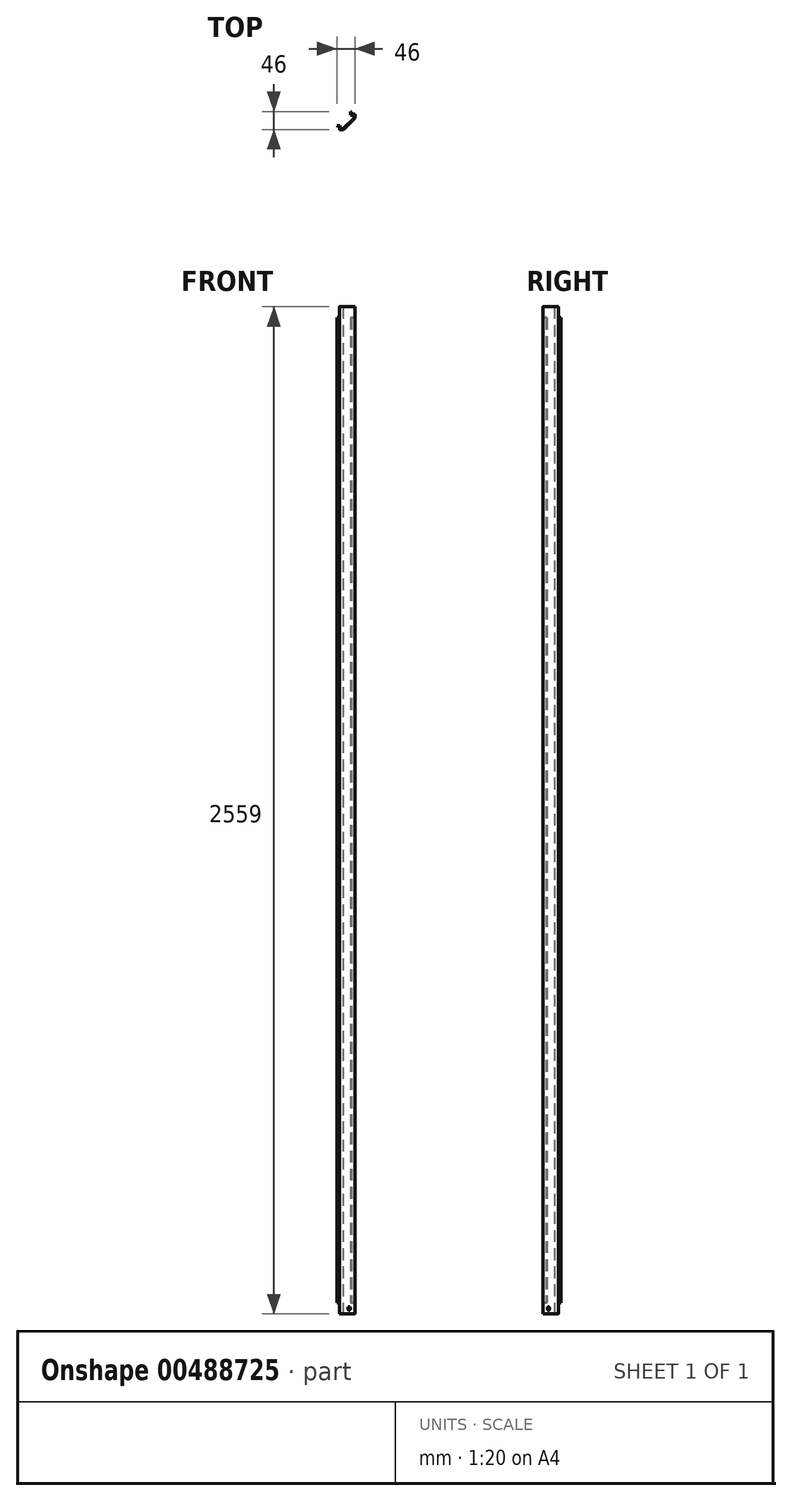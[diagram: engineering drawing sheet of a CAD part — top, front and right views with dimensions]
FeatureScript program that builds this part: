
annotation { "Feature Type Name" : "Feature", "Feature Type Description" : "" }
export const myFeature = defineFeature(function(context is Context, id is Id, definition is map)
    precondition{}
    {
        {
            var Q0;
            Q0=qCreatedBy(makeId("Top.planeOp"),FACE);
            var sketch = newSketch(context, id + "F0", { "sketchPlane" : qUnion([Q0])});
            skLineSegment(sketch, "E0", {"start": v(-68.1, 0) * mm, "end": v(72.16, 0) * mm, "construction": true});
            skLineSegment(sketch, "E1", {"start": v(0, 70.28) * mm, "end": v(0, -61.88) * mm, "construction": true});
            skLineSegment(sketch, "E2.bottom", {"start": v(-19.75, 19.75) * mm, "end": v(19.75, 19.75) * mm, "construction": true});
            skLineSegment(sketch, "E2.top", {"start": v(-19.75, -19.75) * mm, "end": v(19.75, -19.75) * mm, "construction": true});
            skLineSegment(sketch, "E2.left", {"start": v(-19.75, 19.75) * mm, "end": v(-19.75, -19.75) * mm, "construction": true});
            skLineSegment(sketch, "E2.right", {"start": v(19.75, 19.75) * mm, "end": v(19.75, -19.75) * mm, "construction": true});
            skLineSegment(sketch, "E3", {"start": v(-19.75, -19.75) * mm, "end": v(-9.25, -19.75) * mm});
            skLineSegment(sketch, "E4", {"start": v(19.75, 19.75) * mm, "end": v(19.75, 9.25) * mm});
            skLineSegment(sketch, "E5", {"start": v(-9.25, -19.75) * mm, "end": v(19.75, 9.25) * mm});
            skLineSegment(sketch, "E6.0", {"start": v(-19.75, -17.75) * mm, "end": v(-10.08, -17.75) * mm});
            skLineSegment(sketch, "E6.1", {"start": v(-10.08, -17.75) * mm, "end": v(17.75, 10.08) * mm});
            skLineSegment(sketch, "E6.2", {"start": v(17.75, 19.75) * mm, "end": v(17.75, 10.08) * mm});
            skLineSegment(sketch, "E7", {"start": v(-19.75, -19.75) * mm, "end": v(-19.75, -17.75) * mm});
            skLineSegment(sketch, "E8", {"start": v(19.75, 19.75) * mm, "end": v(17.75, 19.75) * mm});
            skSolve(sketch);
        }
        {
            var Q0;
            Q0=qSketchRegion(id+"F0",true);
            extrude(context, id + "F1", {"entities" : qUnion([Q0]), "depth" : 28 * mm});
        }
        {
            var Q0;
            Q0=makeQuery(id+"F1.opExtrude","CAP_FACE",FACE,{"disambiguationData":[OSD([sQuery(id+"F0.wireOp",EDGE,"E3"),sQuery(id+"F0.wireOp",EDGE,"E4"),sQuery(id+"F0.wireOp",EDGE,"E5"),sQuery(id+"F0.wireOp",EDGE,"E6.0"),sQuery(id+"F0.wireOp",EDGE,"E6.1"),sQuery(id+"F0.wireOp",EDGE,"E6.2"),sQuery(id+"F0.wireOp",EDGE,"E7"),sQuery(id+"F0.wireOp",EDGE,"E8")])],"isStart":false});
            var sketch = newSketch(context, id + "F2", { "sketchPlane" : qUnion([Q0])});
            skLineSegment(sketch, "E9.1", {"start": v(-9.25, -19.75) * mm, "end": v(19.75, 9.25) * mm});
            skLineSegment(sketch, "E9.2", {"start": v(19.75, 19.75) * mm, "end": v(19.75, 9.25) * mm});
            skLineSegment(sketch, "E10", {"start": v(19.75, 19.75) * mm, "end": v(11.25, 19.75) * mm});
            skLineSegment(sketch, "E11", {"start": v(17.75, 17.75) * mm, "end": v(17.75, 10.08) * mm});
            skLineSegment(sketch, "E12", {"start": v(17.75, 10.08) * mm, "end": v(16.59, 8.91) * mm});
            skLineSegment(sketch, "E13.left", {"start": v(11.25, 19.75) * mm, "end": v(11.25, 24.25) * mm});
            skLineSegment(sketch, "E14", {"start": v(11.25, 24.25) * mm, "end": v(9.25, 26.25) * mm});
            skLineSegment(sketch, "E15.trimOffspring", {"start": v(16.59, 8.91) * mm, "end": v(-8.91, -16.59) * mm});
            skLineSegment(sketch, "E16.0", {"start": v(9.25, 19.75) * mm, "end": v(9.25, 23.42) * mm});
            skLineSegment(sketch, "E17.0", {"start": v(9.25, 23.42) * mm, "end": v(9.25, 23.42) * mm});
            skLineSegment(sketch, "E18.trimOffspring", {"start": v(9.25, 23.42) * mm, "end": v(9.25, 26.25) * mm});
            skLineSegment(sketch, "E19", {"start": v(0, 0) * mm, "end": v(5.25, -5.25) * mm, "construction": true});
            skLineSegment(sketch, "E20.MirrorCS", {"start": v(-19.75, -9.25) * mm, "end": v(-23.42, -9.25) * mm});
            skLineSegment(sketch, "E21.MirrorCS", {"start": v(-19.75, -11.25) * mm, "end": v(-24.25, -11.25) * mm});
            skLineSegment(sketch, "E22.MirrorCS", {"start": v(-23.42, -9.25) * mm, "end": v(-26.25, -9.25) * mm});
            skLineSegment(sketch, "E23.MirrorCS", {"start": v(-19.75, -19.75) * mm, "end": v(-9.25, -19.75) * mm});
            skLineSegment(sketch, "E24.MirrorCS", {"start": v(-10.08, -17.75) * mm, "end": v(-8.91, -16.59) * mm});
            skLineSegment(sketch, "E25.MirrorCS", {"start": v(-24.25, -11.25) * mm, "end": v(-26.25, -9.25) * mm});
            skLineSegment(sketch, "E26.MirrorCS", {"start": v(-17.75, -17.75) * mm, "end": v(-10.08, -17.75) * mm});
            skLineSegment(sketch, "E27.MirrorCS", {"start": v(-23.42, -9.25) * mm, "end": v(-23.42, -9.25) * mm});
            skLineSegment(sketch, "E28.MirrorCS", {"start": v(-19.75, -19.75) * mm, "end": v(-19.75, -11.25) * mm});
            skLineSegment(sketch, "E29.trimOffspring", {"start": v(-8.91, -16.59) * mm, "end": v(-10.08, -17.75) * mm});
            skLineSegment(sketch, "E30", {"start": v(9.25, 19.75) * mm, "end": v(9.25, 17.75) * mm});
            skLineSegment(sketch, "E31", {"start": v(9.25, 17.75) * mm, "end": v(17.75, 17.75) * mm});
            skLineSegment(sketch, "E32", {"start": v(-19.75, -9.25) * mm, "end": v(-17.75, -9.25) * mm});
            skLineSegment(sketch, "E33", {"start": v(-17.75, -9.25) * mm, "end": v(-17.75, -17.75) * mm});
            skSolve(sketch);
        }
        {
            var Q0;
            Q0=qSketchRegion(id+"F2",true);
            extrude(context, id + "F3", {"entities" : qUnion([Q0]), "operationType" : NewBodyOperationType.ADD, "depth" : 2503 * mm, "offsetDistance" : 25 * mm});
        }
        {
            var Q0;
            Q0=makeQuery(id+"F3.opExtrude","CAP_FACE",FACE,{"disambiguationData":[OSD([sQuery(id+"F2.wireOp",EDGE,"E9.1"),sQuery(id+"F2.wireOp",EDGE,"E9.2"),sQuery(id+"F2.wireOp",EDGE,"E10"),sQuery(id+"F2.wireOp",EDGE,"E11"),sQuery(id+"F2.wireOp",EDGE,"E12"),sQuery(id+"F2.wireOp",EDGE,"E13.left"),sQuery(id+"F2.wireOp",EDGE,"E14"),sQuery(id+"F2.wireOp",EDGE,"E15.trimOffspring"),sQuery(id+"F2.wireOp",EDGE,"E16.0"),sQuery(id+"F2.wireOp",EDGE,"E17.0"),sQuery(id+"F2.wireOp",EDGE,"E18.trimOffspring"),sQuery(id+"F2.wireOp",EDGE,"E20.MirrorCS"),sQuery(id+"F2.wireOp",EDGE,"E21.MirrorCS"),sQuery(id+"F2.wireOp",EDGE,"E22.MirrorCS"),sQuery(id+"F2.wireOp",EDGE,"E23.MirrorCS"),sQuery(id+"F2.wireOp",EDGE,"E25.MirrorCS"),sQuery(id+"F2.wireOp",EDGE,"E26.MirrorCS"),sQuery(id+"F2.wireOp",EDGE,"E27.MirrorCS"),sQuery(id+"F2.wireOp",EDGE,"E28.MirrorCS"),sQuery(id+"F2.wireOp",EDGE,"E29.trimOffspring"),sQuery(id+"F2.wireOp",EDGE,"E30"),sQuery(id+"F2.wireOp",EDGE,"E31"),sQuery(id+"F2.wireOp",EDGE,"E32"),sQuery(id+"F2.wireOp",EDGE,"E33")])],"isStart":false});
            var sketch = newSketch(context, id + "F4", { "sketchPlane" : qUnion([Q0])});
            skLineSegment(sketch, "E34.0.0", {"start": v(19.75, 19.75) * mm, "end": v(19.75, 9.25) * mm});
            skLineSegment(sketch, "E34.0.1", {"start": v(19.75, 9.25) * mm, "end": v(-9.25, -19.75) * mm});
            skLineSegment(sketch, "E34.0.2", {"start": v(-9.25, -19.75) * mm, "end": v(-19.75, -19.75) * mm});
            skLineSegment(sketch, "E34.0.3", {"start": v(-19.75, -19.75) * mm, "end": v(-19.75, -17.75) * mm});
            skLineSegment(sketch, "E34.0.4", {"start": v(-19.75, -17.75) * mm, "end": v(-10.08, -17.75) * mm});
            skLineSegment(sketch, "E34.0.5", {"start": v(-10.08, -17.75) * mm, "end": v(17.75, 10.08) * mm});
            skLineSegment(sketch, "E34.0.6", {"start": v(17.75, 10.08) * mm, "end": v(17.75, 19.75) * mm});
            skLineSegment(sketch, "E34.0.7", {"start": v(17.75, 19.75) * mm, "end": v(19.75, 19.75) * mm});
            skSolve(sketch);
        }
        {
            var Q0;
            Q0 = qSketchRegion(id + "F4", true);
            extrude(context, id + "F5", {"entities" : qUnion([Q0]), "operationType" : NewBodyOperationType.ADD, "depth" : 28 * mm});
        }
        {
            var Q0;
            Q0=makeQuery(id+"F5.boolean.opBoolean","MERGE",EDGE,{"derivedFrom":[makeQuery(id+"F3.boolean.opBoolean","MERGE",EDGE,{"derivedFrom":[makeQuery(id+"F1.opExtrude","SWEPT_EDGE",EDGE,{"disambiguationData":[OSD([sQuery(id+"F0.wireOp",EDGE,"E4"),sQuery(id+"F0.wireOp",EDGE,"E5")])]}),makeQuery(id+"F3.opExtrude","SWEPT_EDGE",EDGE,{"disambiguationData":[OSD([sQuery(id+"F2.wireOp",EDGE,"E9.1"),sQuery(id+"F2.wireOp",EDGE,"E9.2")])]})]}),makeQuery(id+"F5.opExtrude","SWEPT_EDGE",EDGE,{"disambiguationData":[OSD([sQuery(id+"F4.wireOp",EDGE,"E34.0.0"),sQuery(id+"F4.wireOp",EDGE,"E34.0.1")])]})]});
            var Q1;
            Q1=makeQuery(id+"F5.boolean.opBoolean","MERGE",EDGE,{"derivedFrom":[makeQuery(id+"F3.boolean.opBoolean","MERGE",EDGE,{"derivedFrom":[makeQuery(id+"F1.opExtrude","SWEPT_EDGE",EDGE,{"disambiguationData":[OSD([sQuery(id+"F0.wireOp",EDGE,"E3"),sQuery(id+"F0.wireOp",EDGE,"E5")])]}),makeQuery(id+"F3.opExtrude","SWEPT_EDGE",EDGE,{"disambiguationData":[OSD([sQuery(id+"F2.wireOp",EDGE,"E9.1"),sQuery(id+"F2.wireOp",EDGE,"E23.MirrorCS")])]})]}),makeQuery(id+"F5.opExtrude","SWEPT_EDGE",EDGE,{"disambiguationData":[OSD([sQuery(id+"F4.wireOp",EDGE,"E34.0.1"),sQuery(id+"F4.wireOp",EDGE,"E34.0.2")])]})]});
            fillet(context, id + "F6", {"entities" : qUnion([Q0, Q1]), "radius" : 2 * mm, "tangentPropagation" : true, "allowEdgeOverflow" : false});
        }
        {
            var Q0;
            Q0=makeQuery(id+"F5.boolean.opBoolean","MERGE",EDGE,{"derivedFrom":[makeQuery(id+"F3.boolean.opBoolean","MERGE",EDGE,{"derivedFrom":[makeQuery(id+"F1.opExtrude","SWEPT_EDGE",EDGE,{"disambiguationData":[OSD([sQuery(id+"F0.wireOp",EDGE,"E3"),sQuery(id+"F0.wireOp",EDGE,"E7")])]}),makeQuery(id+"F3.opExtrude","SWEPT_EDGE",EDGE,{"disambiguationData":[OSD([sQuery(id+"F2.wireOp",EDGE,"E23.MirrorCS"),sQuery(id+"F2.wireOp",EDGE,"E28.MirrorCS")])]})]}),makeQuery(id+"F5.opExtrude","SWEPT_EDGE",EDGE,{"disambiguationData":[OSD([sQuery(id+"F4.wireOp",EDGE,"E34.0.2"),sQuery(id+"F4.wireOp",EDGE,"E34.0.3")])]})]});
            var Q1;
            Q1=makeQuery(id+"F5.boolean.opBoolean","MERGE",EDGE,{"derivedFrom":[makeQuery(id+"F3.boolean.opBoolean","MERGE",EDGE,{"derivedFrom":[makeQuery(id+"F1.opExtrude","SWEPT_EDGE",EDGE,{"disambiguationData":[OSD([sQuery(id+"F0.wireOp",EDGE,"E4"),sQuery(id+"F0.wireOp",EDGE,"E8")])]}),makeQuery(id+"F3.opExtrude","SWEPT_EDGE",EDGE,{"disambiguationData":[OSD([sQuery(id+"F2.wireOp",EDGE,"E9.2"),sQuery(id+"F2.wireOp",EDGE,"E10")])]})]}),makeQuery(id+"F5.opExtrude","SWEPT_EDGE",EDGE,{"disambiguationData":[OSD([sQuery(id+"F4.wireOp",EDGE,"E34.0.0"),sQuery(id+"F4.wireOp",EDGE,"E34.0.7")])]})]});
            fillet(context, id + "F7", {"entities" : qUnion([Q0, Q1]), "radius" : 1 * mm, "tangentPropagation" : true, "allowEdgeOverflow" : false});
        }
        {
            var Q0;
            Q0=makeQuery(id+"F5.boolean.opBoolean","MERGE",FACE,{"derivedFrom":[makeQuery(id+"F3.boolean.opBoolean","MERGE",FACE,{"derivedFrom":[makeQuery(id+"F1.opExtrude","SWEPT_FACE",FACE,{"disambiguationData":[OSD([sQuery(id+"F0.wireOp",EDGE,"E5")])]}),makeQuery(id+"F3.opExtrude","SWEPT_FACE",FACE,{"disambiguationData":[OSD([sQuery(id+"F2.wireOp",EDGE,"E9.1")])]})]}),makeQuery(id+"F5.opExtrude","SWEPT_FACE",FACE,{"disambiguationData":[OSD([sQuery(id+"F4.wireOp",EDGE,"E34.0.1")])]})]});
            var sketch = newSketch(context, id + "F8", { "sketchPlane" : qUnion([Q0])});
            skLineSegment(sketch, "E35.0", {"start": v(19.1, 28) * mm, "end": v(25.1, 28) * mm});
            skPoint(sketch, "E35.1", {"position": v(22.1, 28) * mm});
            skLineSegment(sketch, "E36", {"start": v(19.1, 28) * mm, "end": v(-29.4, 28) * mm});
            skLineSegment(sketch, "E37", {"start": v(0, 0) * mm, "end": v(0, 28) * mm, "construction": true});
            skCircle(sketch, "E38", {"center": v(0, 14) * mm, "radius": 4.25 * mm});
            skSolve(sketch);
        }
        {
            var Q0;
            Q0 = qSketchRegion(id + "F8", true);
            extrude(context, id + "F9", {"entities" : qUnion([Q0]), "operationType" : NewBodyOperationType.REMOVE, "oppositeDirection" : true, "depth" : 25 * mm, "offsetDistance" : 25 * mm});
        }
    });
